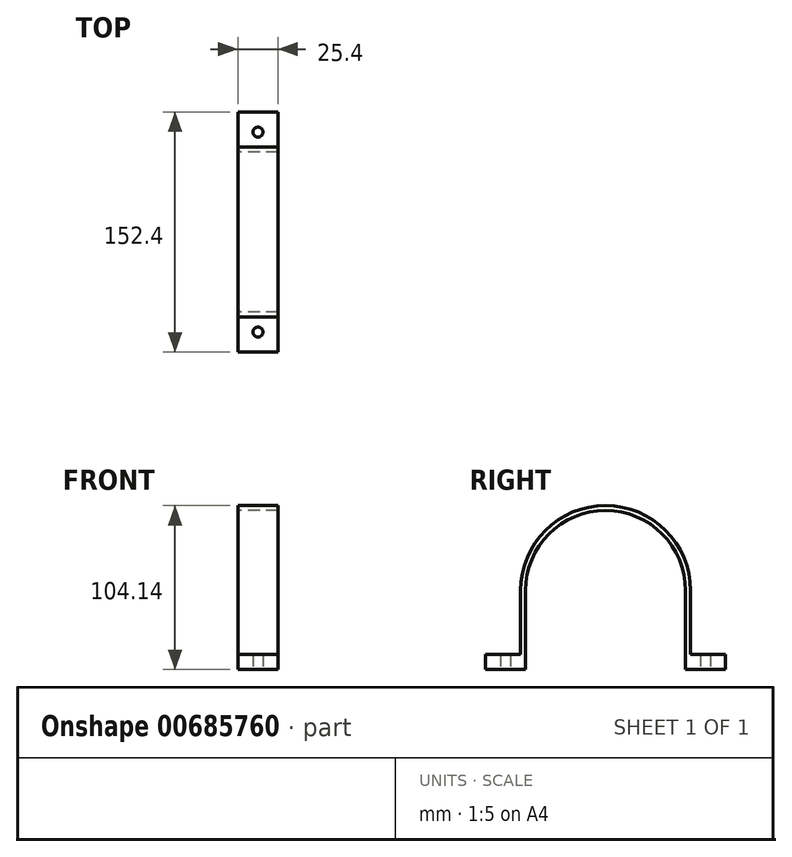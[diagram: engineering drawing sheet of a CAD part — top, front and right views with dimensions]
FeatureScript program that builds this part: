
annotation { "Feature Type Name" : "Feature", "Feature Type Description" : "" }
export const myFeature = defineFeature(function(context is Context, id is Id, definition is map)
    precondition{}
    {
        {
            var Q0;
            Q0=qCreatedBy(makeId("Right.planeOp"),FACE);
            var sketch = newSketch(context, id + "F0", { "sketchPlane" : qUnion([Q0])});
            skLineSegment(sketch, "E0.bottom", {"start": v(-73.88, -4.76) * mm, "end": v(-99.28, -4.76) * mm});
            skLineSegment(sketch, "E0.top", {"start": v(-73.88, 4.76) * mm, "end": v(-99.28, 4.76) * mm});
            skLineSegment(sketch, "E0.left", {"start": v(-73.88, -4.76) * mm, "end": v(-73.88, 4.76) * mm});
            skLineSegment(sketch, "E0.right", {"start": v(-99.28, -4.76) * mm, "end": v(-99.28, 4.76) * mm});
            skPoint(sketch, "E0.middle", {"position": v(-86.58, 0) * mm});
            skLineSegment(sketch, "E1.bottom", {"start": v(53.12, -4.76) * mm, "end": v(27.72, -4.76) * mm});
            skLineSegment(sketch, "E1.top", {"start": v(53.12, 4.76) * mm, "end": v(27.72, 4.76) * mm});
            skLineSegment(sketch, "E1.left", {"start": v(53.12, -4.76) * mm, "end": v(53.12, 4.76) * mm});
            skLineSegment(sketch, "E1.right", {"start": v(27.72, -4.76) * mm, "end": v(27.72, 4.76) * mm});
            skPoint(sketch, "E1.middle", {"position": v(40.42, 0) * mm});
            skLineSegment(sketch, "E2", {"start": v(-73.88, 4.76) * mm, "end": v(-73.88, 45.4) * mm});
            skLineSegment(sketch, "E3", {"start": v(27.72, 4.76) * mm, "end": v(27.72, 45.4) * mm});
            skArc(sketch, "E4", {"start": v(-73.88, 45.4) * mm, "mid": v(-23.08, 96.2) * mm, "end": v(27.72, 45.4) * mm});
            skArc(sketch, "E5.1", {"start": v(-77.06, 45.4) * mm, "mid": v(-23.08, 99.38) * mm, "end": v(30.9, 45.4) * mm});
            skLineSegment(sketch, "E6", {"start": v(30.9, 45.4) * mm, "end": v(30.9, -4.76) * mm});
            skLineSegment(sketch, "E7", {"start": v(-77.06, 45.4) * mm, "end": v(-77.06, -4.76) * mm});
            skSolve(sketch);
        }
        {
            var Q0;
            {var subQ0=sQuery(id+"F0.wireOp",EDGE,"E0.right");Q0=makeQuery(id+"F0.imprint","IMPRINT",FACE,{"disambiguationData":[TD([[makeQuery(id+"F0.imprint","IMPRINT",EDGE,{"derivedFrom":subQ0}),-1.0]])]});}
            var Q1;
            {var subQ0=sQuery(id+"F0.wireOp",EDGE,"E0.left");Q1=makeQuery(id+"F0.imprint","IMPRINT",FACE,{"disambiguationData":[TD([[makeQuery(id+"F0.imprint","IMPRINT",EDGE,{"derivedFrom":subQ0}),1.0]])]});}
            var Q2;
            {var subQ0=sQuery(id+"F0.wireOp",EDGE,"E2");Q2=makeQuery(id+"F0.imprint","IMPRINT",FACE,{"disambiguationData":[TD([[makeQuery(id+"F0.imprint","IMPRINT",EDGE,{"derivedFrom":subQ0}),1.0]])]});}
            var Q3;
            Q3=makeQuery(id+"F0.imprint","IMPRINT",FACE,{"disambiguationData":[TD([[makeQuery(id+"F0.imprint","IMPRINT",EDGE,{"derivedFrom":sQuery(id+"F0.wireOp",EDGE,"E1.bottom")}),-1.0]])]});
            extrude(context, id + "F1", {"entities" : qUnion([Q0, Q1, Q2, Q3]), "endBound" : BoundingType.SYMMETRIC, "depth" : 25.4 * mm});
        }
        {
            var Q0;
            Q0=makeQuery(id+"F1.opExtrude","SWEPT_FACE",FACE,{"disambiguationData":[OSD([sQuery(id+"F0.wireOp",EDGE,"E1.bottom")])]});
            var sketch = newSketch(context, id + "F2", { "sketchPlane" : qUnion([Q0])});
            skPoint(sketch, "E8", {"position": v(0, -40.42) * mm});
            skCircle(sketch, "E9", {"center": v(0, -40.42) * mm, "radius": 3.18 * mm});
            skSolve(sketch);
        }
        {
            var Q0;
            Q0=makeQuery(id+"F2.imprint","IMPRINT",FACE,{"disambiguationData":[TD([[makeQuery(id+"F2.imprint","IMPRINT",EDGE,{"derivedFrom":sQuery(id+"F2.wireOp",EDGE,"E9")}),1.0]])]});
            extrude(context, id + "F3", {"entities" : qUnion([Q0]), "oppositeDirection" : true, "depth" : 9.52 * mm});
        }
        {
            var Q0;
            Q0=makeQuery(id+"F1.opExtrude","SWEPT_FACE",FACE,{"disambiguationData":[OSD([sQuery(id+"F0.wireOp",EDGE,"E0.bottom")])]});
            var sketch = newSketch(context, id + "F4", { "sketchPlane" : qUnion([Q0])});
            skPoint(sketch, "E10", {"position": v(0, 86.58) * mm});
            skCircle(sketch, "E11", {"center": v(0, 86.58) * mm, "radius": 3.18 * mm});
            skSolve(sketch);
        }
        {
            var Q0;
            Q0=makeQuery(id+"F4.imprint","IMPRINT",FACE,{"disambiguationData":[TD([[makeQuery(id+"F4.imprint","IMPRINT",EDGE,{"derivedFrom":sQuery(id+"F4.wireOp",EDGE,"E11")}),1.0]])]});
            extrude(context, id + "F5", {"entities" : qUnion([Q0]), "oppositeDirection" : true, "depth" : 9.52 * mm});
        }
    });
